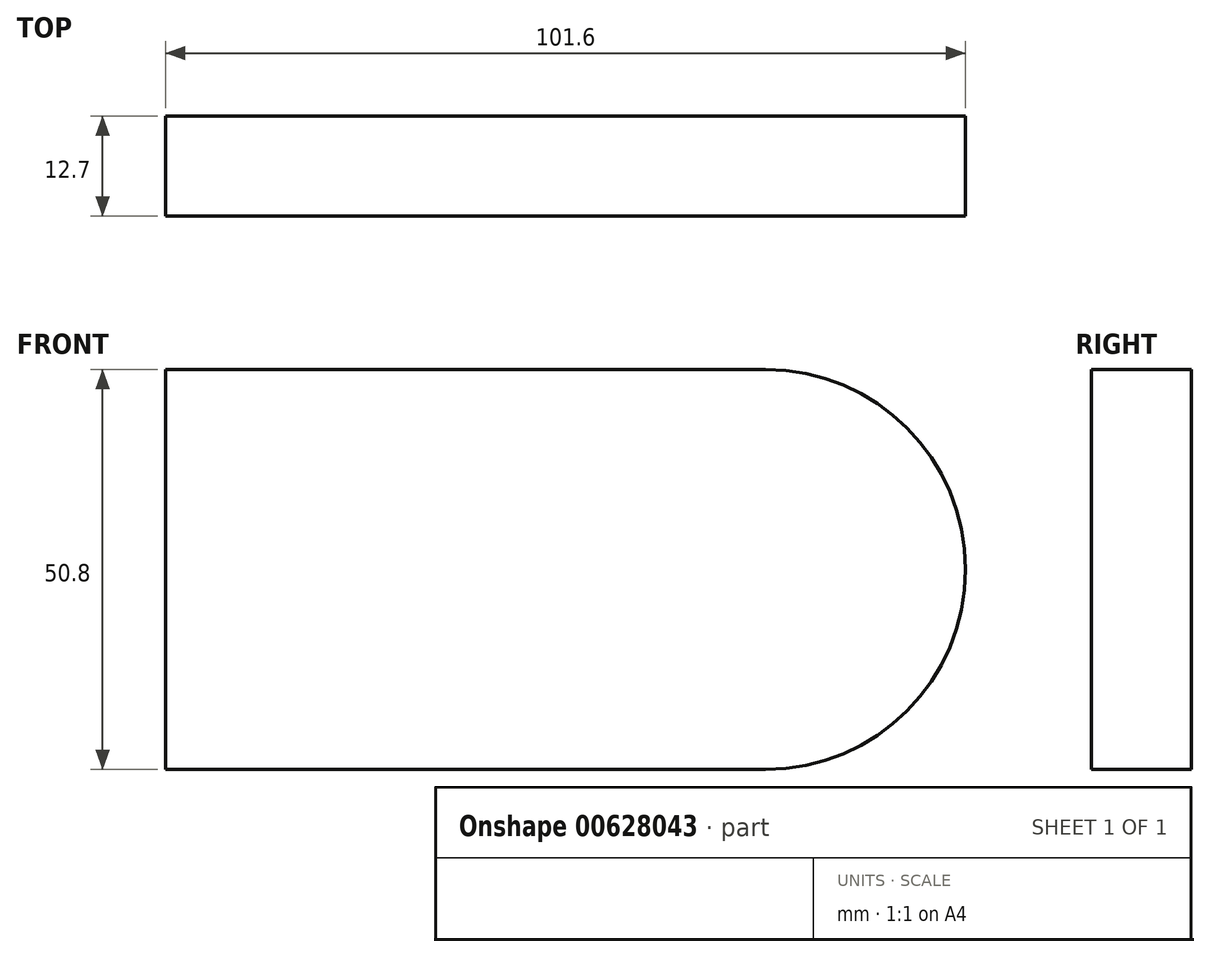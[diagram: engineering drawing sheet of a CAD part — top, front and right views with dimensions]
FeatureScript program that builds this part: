
annotation { "Feature Type Name" : "Feature", "Feature Type Description" : "" }
export const myFeature = defineFeature(function(context is Context, id is Id, definition is map)
    precondition{}
    {
        {
            var Q0;
            Q0=qCreatedBy(makeId("Front.planeOp"),FACE);
            var sketch = newSketch(context, id + "F0", { "sketchPlane" : qUnion([Q0])});
            skLineSegment(sketch, "E0.bottom", {"start": v(-48.47, 48.47) * mm, "end": v(27.73, 48.47) * mm});
            skLineSegment(sketch, "E0.top", {"start": v(-48.47, -2.33) * mm, "end": v(27.73, -2.33) * mm});
            skLineSegment(sketch, "E0.left", {"start": v(-48.47, 48.47) * mm, "end": v(-48.47, -2.33) * mm});
            skArc(sketch, "E1", {"start": v(27.73, -2.33) * mm, "mid": v(53.13, 23.07) * mm, "end": v(27.73, 48.47) * mm});
            skSolve(sketch);
        }
        {
            var Q0;
            Q0 = qSketchRegion(id + "F0", true);
            extrude(context, id + "F1", {"entities" : qUnion([Q0]), "depth" : 12.7 * mm, "offsetDistance" : 25.4 * mm});
        }
    });
